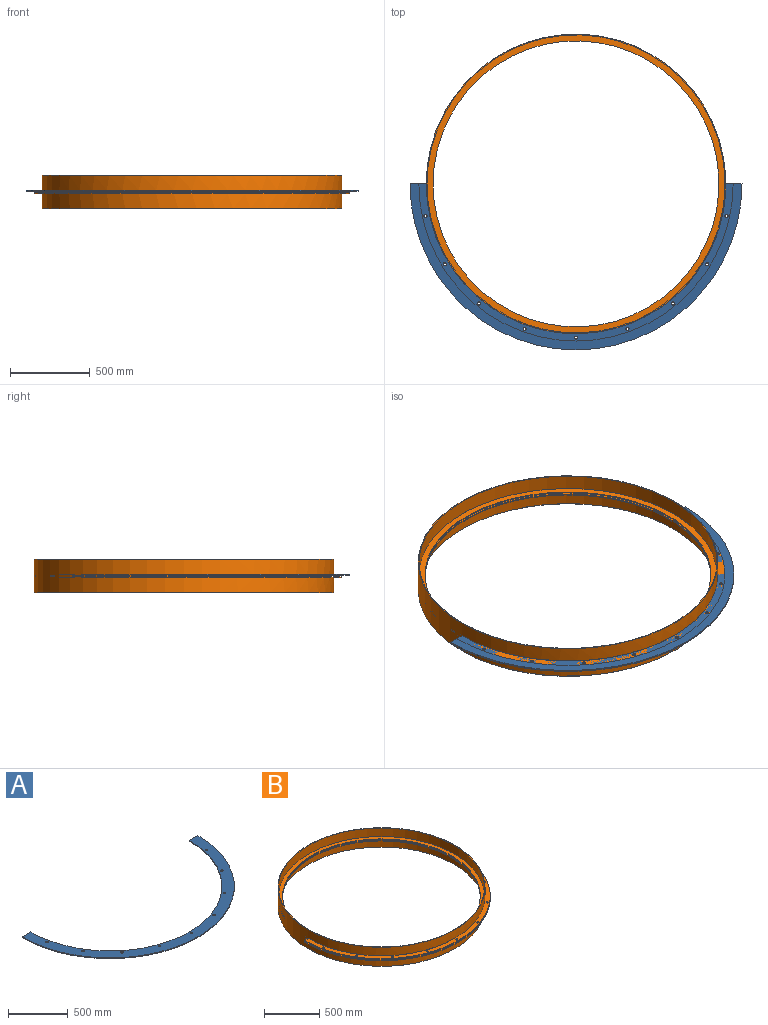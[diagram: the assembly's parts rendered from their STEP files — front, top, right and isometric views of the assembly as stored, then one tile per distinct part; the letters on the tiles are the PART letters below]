
ASSEMBLY  parts=2 mates=1
PART A: 15 faces, bbox 2082.8x1041.4x7.9 mm
  f0: plane 2082.8x1041.4mm, normal (0,0,-1), area 313174.9mm2, adj f2,f3,f4,f5,f6,f7,f8,f9
  f1: plane 2082.8x1041.4mm, normal (0,0,1), area 313174.9mm2, adj f2,f3,f4,f5,f6,f7,f8,f9
  f2: cylinder r=939.8mm len=1879.6mm, axis (0,0,1), area 23435.2mm2, adj f0,f1,f3,f5
  f3: plane 101.6x7.94mm, normal (0,1,0), area 806.5mm2, adj f0,f1,f2,f4
  f4: cylinder r=1041.4mm len=2082.8mm, axis (0,0,1), area 25968.8mm2, adj f0,f1,f3,f5
  f5: plane 101.6x7.94mm, normal (0,1,0), area 806.5mm2, adj f0,f1,f2,f4
  f6: cylinder r=10.32mm len=20.64mm, axis (0,0,1), area 514.6mm2, adj f0,f1
  f7: cylinder r=10.32mm len=20.64mm, axis (0,0,1), area 514.6mm2, adj f0,f1
  f8: cylinder r=10.32mm len=20.64mm, axis (0,0,1), area 514.6mm2, adj f0,f1
  f9: cylinder r=10.32mm len=20.64mm, axis (0,0,1), area 514.6mm2, adj f0,f1
  f10: cylinder r=10.32mm len=20.64mm, axis (0,0,1), area 514.6mm2, adj f0,f1
  f11: cylinder r=10.32mm len=20.64mm, axis (0,0,1), area 514.6mm2, adj f0,f1
  f12: cylinder r=10.32mm len=20.64mm, axis (0,0,1), area 514.6mm2, adj f0,f1
  f13: cylinder r=10.32mm len=20.64mm, axis (0,0,1), area 514.6mm2, adj f0,f1
  f14: cylinder r=10.32mm len=20.64mm, axis (0,0,1), area 514.6mm2, adj f0,f1
PART B: 40 faces, bbox 1971.7x1925.6x211.3 mm
  f0: plane 1971.68x1920.88mm, normal (0,0,-1), area 370401.2mm2, adj f3,f4,f5,f9,f10,f11,f12,f13
  f1: plane 1971.68x985.84mm, normal (0,0,1), area 137098mm2, adj f2,f10,f11,f12,f13,f14,f15,f16
  f2: cylinder r=939.8mm len=1879.6mm, axis (0,0,-1), area 1182365.9mm2, adj f1,f3,f4,f6,f10,f12,f23,f24
  f3: plane 9.53x4.76mm, normal (0,-1,0), area 45.4mm2, adj f0,f2,f5,f22
  f4: plane 9.53x4.76mm, normal (0,-1,0), area 45.4mm2, adj f0,f2,f5,f22
  f5: cylinder r=935.04mm len=1870.08mm, axis (0,0,-1), area 27979.8mm2, adj f0,f3,f4,f22
  f6: plane 1879.6x1879.6mm, normal (0,0,1), area 28051mm2, adj f2,f7
  f7: cylinder r=935.04mm len=1870.08mm, axis (0,0,-1), area 555544mm2, adj f6,f8
  f8: plane 1870.08x1870.08mm, normal (0,0,1), area 219277.7mm2, adj f7,f9
  f9: cylinder r=896.94mm len=1793.88mm, axis (0,0,-1), area 35786.2mm2, adj f0,f8
  f10: plane 46.04x6.35mm, normal (0,1,0), area 292.3mm2, adj f0,f1,f2,f11
  f11: cylinder r=985.84mm len=1971.68mm, axis (0,0,-1), area 19666.6mm2, adj f0,f1,f10,f12
  f12: plane 46.04x6.35mm, normal (0,1,0), area 292.3mm2, adj f0,f1,f2,f11
  f13: cylinder r=8.73mm len=17.46mm, axis (0,0,-1), area 348.4mm2, adj f0,f1
  f14: cylinder r=8.73mm len=17.46mm, axis (0,0,-1), area 348.4mm2, adj f0,f1
  f15: cylinder r=8.73mm len=17.46mm, axis (0,0,-1), area 348.4mm2, adj f0,f1
  f16: cylinder r=8.73mm len=17.46mm, axis (0,0,-1), area 348.4mm2, adj f0,f1
  f17: cylinder r=8.73mm len=17.46mm, axis (0,0,-1), area 348.4mm2, adj f0,f1
  f18: cylinder r=8.73mm len=17.46mm, axis (0,0,-1), area 348.4mm2, adj f0,f1
  f19: cylinder r=8.73mm len=17.46mm, axis (0,0,-1), area 348.4mm2, adj f0,f1
  f20: cylinder r=8.73mm len=17.46mm, axis (0,0,-1), area 348.4mm2, adj f0,f1
  f21: cylinder r=8.73mm len=17.46mm, axis (0,0,-1), area 348.4mm2, adj f0,f1
  f22: plane 1971.68x1920.88mm, normal (0,0,1), area 370401.2mm2, adj f3,f4,f5,f27,f28,f29,f30,f31
  f23: plane 1971.68x985.84mm, normal (0,0,-1), area 137098mm2, adj f2,f28,f29,f30,f31,f32,f33,f34
  f24: plane 1879.6x1879.6mm, normal (0,0,-1), area 28051mm2, adj f2,f25
  f25: cylinder r=935.04mm len=1870.08mm, axis (0,0,1), area 555544mm2, adj f24,f26
  f26: plane 1870.08x1870.08mm, normal (0,0,-1), area 219277.7mm2, adj f25,f27
  f27: cylinder r=896.94mm len=1793.88mm, axis (0,0,1), area 35786.2mm2, adj f22,f26
  f28: plane 46.04x6.35mm, normal (0,1,0), area 292.3mm2, adj f2,f22,f23,f29
  f29: cylinder r=985.84mm len=1971.68mm, axis (0,0,1), area 19666.6mm2, adj f22,f23,f28,f30
  f30: plane 46.04x6.35mm, normal (0,1,0), area 292.3mm2, adj f2,f22,f23,f29
  f31: cylinder r=8.73mm len=17.46mm, axis (0,0,1), area 348.4mm2, adj f22,f23
  f32: cylinder r=8.73mm len=17.46mm, axis (0,0,1), area 348.4mm2, adj f22,f23
  f33: cylinder r=8.73mm len=17.46mm, axis (0,0,1), area 348.4mm2, adj f22,f23
  f34: cylinder r=8.73mm len=17.46mm, axis (0,0,1), area 348.4mm2, adj f22,f23
  f35: cylinder r=8.73mm len=17.46mm, axis (0,0,1), area 348.4mm2, adj f22,f23
  f36: cylinder r=8.73mm len=17.46mm, axis (0,0,1), area 348.4mm2, adj f22,f23
  f37: cylinder r=8.73mm len=17.46mm, axis (0,0,1), area 348.4mm2, adj f22,f23
  f38: cylinder r=8.73mm len=17.46mm, axis (0,0,1), area 348.4mm2, adj f22,f23
  f39: cylinder r=8.73mm len=17.46mm, axis (0,0,1), area 348.4mm2, adj f22,f23
PLACE A t=(-468.38,1019.51,-119.54)mm
PLACE B t=(-468.38,1019.51,-130.65)mm
MATE cylindrical B.f17 <-> A.f14  axis (0,0,1) through (-468.38,54.31,-119.54)mm
